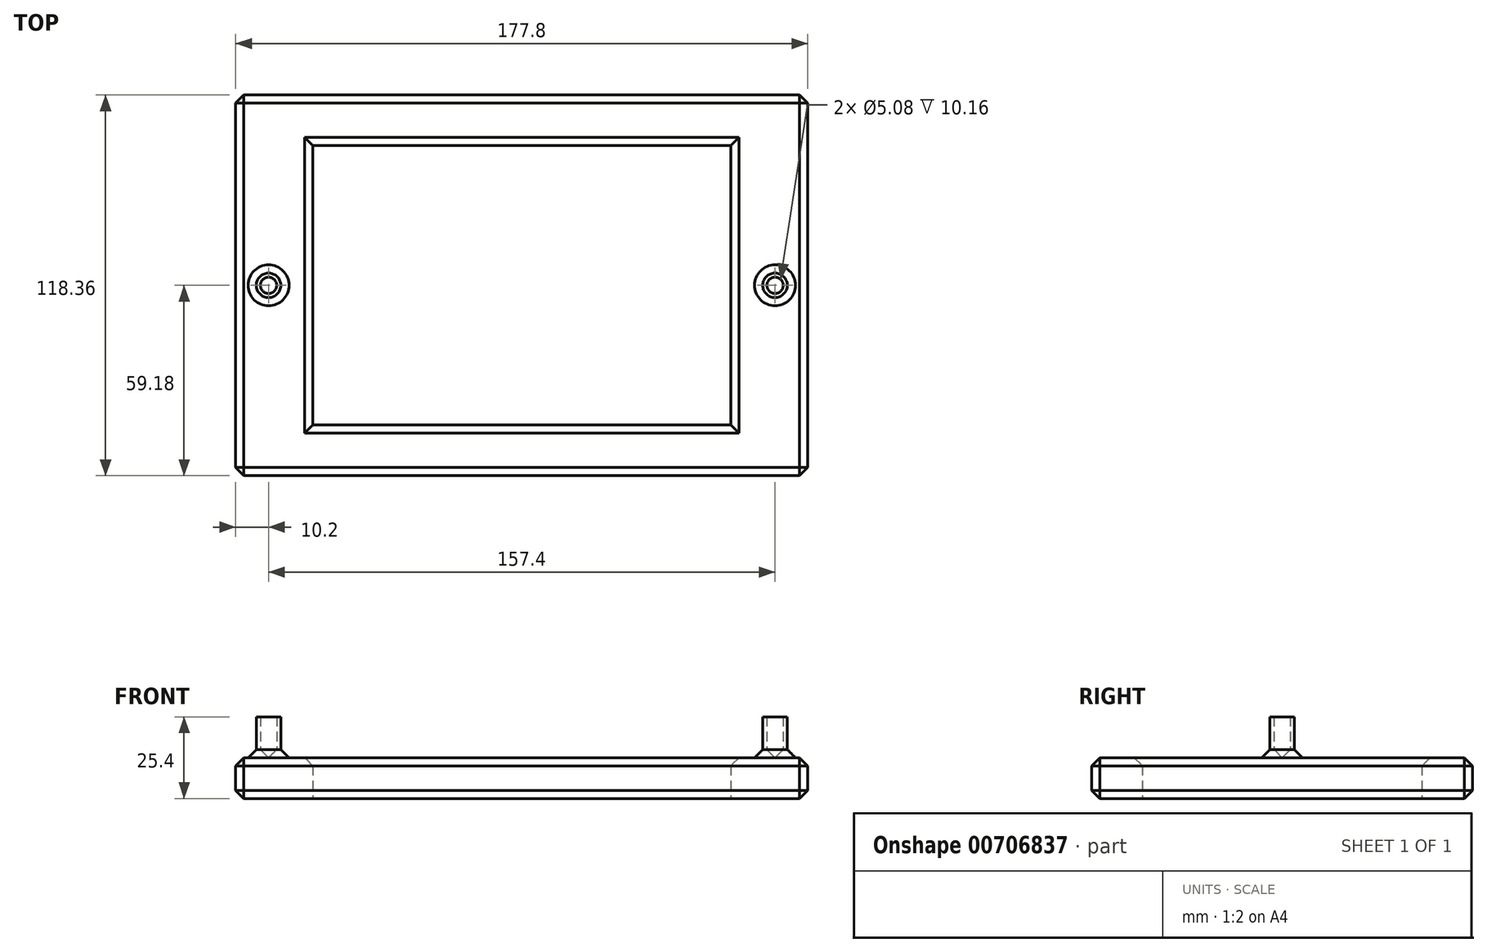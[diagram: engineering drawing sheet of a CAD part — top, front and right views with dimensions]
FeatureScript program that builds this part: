
annotation { "Feature Type Name" : "Feature", "Feature Type Description" : "" }
export const myFeature = defineFeature(function(context is Context, id is Id, definition is map)
    precondition{}
    {
        {
            var Q0;
            Q0=qCreatedBy(makeId("Top.planeOp"),FACE);
            var sketch = newSketch(context, id + "F0", { "sketchPlane" : qUnion([Q0])});
            skLineSegment(sketch, "E0.bottom", {"start": v(-88.9, 59.18) * mm, "end": v(88.9, 59.18) * mm});
            skLineSegment(sketch, "E0.top", {"start": v(-88.9, -59.18) * mm, "end": v(88.9, -59.18) * mm});
            skLineSegment(sketch, "E0.left", {"start": v(-88.9, 59.18) * mm, "end": v(-88.9, -59.18) * mm});
            skLineSegment(sketch, "E0.right", {"start": v(88.9, 59.18) * mm, "end": v(88.9, -59.18) * mm});
            skPoint(sketch, "E0.middle", {"position": v(0, 0) * mm});
            skSolve(sketch);
        }
        {
            var Q0;
            Q0=qCreatedBy(makeId("Top.planeOp"),FACE);
            var sketch = newSketch(context, id + "F1", { "sketchPlane" : qUnion([Q0])});
            skPoint(sketch, "E1.middle", {"position": v(0, 0) * mm});
            skLineSegment(sketch, "E2.bottom", {"start": v(-64.92, 43.43) * mm, "end": v(64.92, 43.43) * mm});
            skLineSegment(sketch, "E2.top", {"start": v(-64.92, -43.43) * mm, "end": v(64.92, -43.43) * mm});
            skLineSegment(sketch, "E2.left", {"start": v(-64.92, 43.43) * mm, "end": v(-64.92, -43.43) * mm});
            skLineSegment(sketch, "E2.right", {"start": v(64.92, 43.43) * mm, "end": v(64.92, -43.43) * mm});
            skSolve(sketch);
        }
        {
            var Q0;
            Q0=qSketchRegion(id+"F0",true);
            extrude(context, id + "F2", {"entities" : qUnion([Q0]), "depth" : 12.7 * mm, "offsetDistance" : 25.4 * mm});
        }
        {
            var Q0;
            Q0=qSketchRegion(id+"F1",true);
            extrude(context, id + "F3", {"entities" : qUnion([Q0]), "operationType" : NewBodyOperationType.REMOVE, "endBound" : BoundingType.UP_TO_NEXT, "depth" : 25.4 * mm, "offsetDistance" : 12.7 * mm});
        }
        {
            var Q0;
            Q0=makeQuery(id+"F2.opExtrude","CAP_FACE",FACE,{"disambiguationData":[OSD([sQuery(id+"F0.wireOp",EDGE,"E0.bottom"),sQuery(id+"F0.wireOp",EDGE,"E0.top"),sQuery(id+"F0.wireOp",EDGE,"E0.left"),sQuery(id+"F0.wireOp",EDGE,"E0.right")])],"isStart":false});
            var sketch = newSketch(context, id + "F4", { "sketchPlane" : qUnion([Q0])});
            skCircle(sketch, "E3", {"center": v(78.7, 0) * mm, "radius": 2.54 * mm});
            skCircle(sketch, "E4", {"center": v(78.7, 0) * mm, "radius": 3.81 * mm});
            skCircle(sketch, "E5.MirrorC", {"center": v(-78.7, 0) * mm, "radius": 3.81 * mm});
            skCircle(sketch, "E6.MirrorC", {"center": v(-78.7, 0) * mm, "radius": 2.54 * mm});
            skSolve(sketch);
        }
        {
            var Q0;
            Q0=makeQuery(id+"F4.imprint","IMPRINT",FACE,{"disambiguationData":[TD([[makeQuery(id+"F4.imprint","IMPRINT",EDGE,{"derivedFrom":sQuery(id+"F4.wireOp",EDGE,"E3")}),1.0]])]});
            extrude(context, id + "F5", {"entities" : qUnion([Q0]), "operationType" : NewBodyOperationType.REMOVE, "depth" : 25.4 * mm, "offsetDistance" : 25.4 * mm});
        }
        {
            var Q0;
            Q0=qSketchRegion(id+"F4",true);
            extrude(context, id + "F6", {"entities" : qUnion([Q0]), "operationType" : NewBodyOperationType.ADD, "depth" : 12.7 * mm, "offsetDistance" : 25.4 * mm});
        }
        {
            var Q0;
            Q0=makeQuery(id+"F2.opExtrude","CAP_FACE",FACE,{"disambiguationData":[OSD([sQuery(id+"F0.wireOp",EDGE,"E0.bottom"),sQuery(id+"F0.wireOp",EDGE,"E0.top"),sQuery(id+"F0.wireOp",EDGE,"E0.left"),sQuery(id+"F0.wireOp",EDGE,"E0.right")])],"isStart":false});
            var Q1;
            Q1=makeQuery(id+"F2.opExtrude","SWEPT_FACE",FACE,{"disambiguationData":[OSD([sQuery(id+"F0.wireOp",EDGE,"E0.bottom")])]});
            var Q2;
            Q2=makeQuery(id+"F2.opExtrude","SWEPT_EDGE",EDGE,{"disambiguationData":[OSD([sQuery(id+"F0.wireOp",EDGE,"E0.top"),sQuery(id+"F0.wireOp",EDGE,"E0.right")])]});
            var Q3;
            Q3=makeQuery(id+"F2.opExtrude","SWEPT_EDGE",EDGE,{"disambiguationData":[OSD([sQuery(id+"F0.wireOp",EDGE,"E0.top"),sQuery(id+"F0.wireOp",EDGE,"E0.left")])]});
            var Q4;
            Q4=makeQuery(id+"F2.opExtrude","CAP_EDGE",EDGE,{"disambiguationData":[OSD([sQuery(id+"F0.wireOp",EDGE,"E0.right")])],"isStart":true});
            var Q5;
            Q5=makeQuery(id+"F2.opExtrude","CAP_EDGE",EDGE,{"disambiguationData":[OSD([sQuery(id+"F0.wireOp",EDGE,"E0.top")])],"isStart":true});
            var Q6;
            Q6=makeQuery(id+"F2.opExtrude","CAP_EDGE",EDGE,{"disambiguationData":[OSD([sQuery(id+"F0.wireOp",EDGE,"E0.left")])],"isStart":true});
            var Q7;
            Q7=makeQuery(id+"F3.boolean.opBoolean","COPY",EDGE,{"derivedFrom":makeQuery(id+"F3.opExtrude","CAP_EDGE",EDGE,{"disambiguationData":[OSD([sQuery(id+"F1.wireOp",EDGE,"E2.right")])],"isStart":true})});
            var Q8;
            Q8=makeQuery(id+"F3.boolean.opBoolean","COPY",EDGE,{"derivedFrom":makeQuery(id+"F3.opExtrude","CAP_EDGE",EDGE,{"disambiguationData":[OSD([sQuery(id+"F1.wireOp",EDGE,"E2.bottom")])],"isStart":true})});
            var Q9;
            Q9=makeQuery(id+"F3.boolean.opBoolean","COPY",EDGE,{"derivedFrom":makeQuery(id+"F3.opExtrude","CAP_EDGE",EDGE,{"disambiguationData":[OSD([sQuery(id+"F1.wireOp",EDGE,"E2.top")])],"isStart":true})});
            var Q10;
            Q10=makeQuery(id+"F3.boolean.opBoolean","COPY",EDGE,{"derivedFrom":makeQuery(id+"F3.opExtrude","CAP_EDGE",EDGE,{"disambiguationData":[OSD([sQuery(id+"F1.wireOp",EDGE,"E2.left")])],"isStart":true})});
            chamfer(context, id + "F7", {"entities" : qUnion([Q0, Q1, Q2, Q3, Q4, Q5, Q6, Q7, Q8, Q9, Q10]), "width" : 2.54 * mm, "tangentPropagation" : true});
        }
    });
